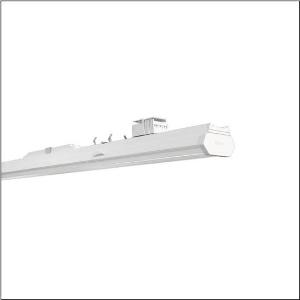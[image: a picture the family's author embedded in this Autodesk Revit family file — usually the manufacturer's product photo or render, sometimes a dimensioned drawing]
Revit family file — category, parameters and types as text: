
# Revit family: licross_r__21_protected_ho_52td11dn4axs_7332
name_source: partatom
category: Lighting Fixtures
units: mm (PartAtom-declared; Revit-internal decimal feet)

## family parameters
Cut with Voids When Loaded = No
Host = Face
Light Source = No
Part Type = Normal
Room Calculation Point = No
Round Connector Dimension = Use Diameter
Shared = No

## types (1)
- --- (1 x LED, 10000 lm, 55.1 W, 4000K)
    Apparent Load = 55 VA
    CIE Flux Codes = 84 94 98 99 100
    Color Rendering = 80
    Color Temperature = 4000K
    Default Elevation = 1800 mm
    Description = Licross® 21 Protected HO, luminaire insert, of sheet steel, galvanised, coil coated, white, length: 1.500mm, width: 90mm, height: 103mm, LED rated luminous flux: 10.000lm, light colour: 840, control gear: DALI 2, with plug, 5-pole, with phase selection, mains connection: 220..240V, AC, 50/60Hz, rated input power: 55W, halogen-free wiring, primary light control with lens, of plastic, primary optical cover: cover, of PMMA, light emission: direct distribution, primary light characteristic: symmetric, protection rating (complete): IP54, insulation class (complete): insulation class I (protective earthing), certification: CE, ENEC, VDE, UKCA, protection symbol: D if used in an environment with non-conductive dust loads with corresponding accessories, impact resistance: IK06, permissible ambient temperature for indoor applications: -25..+45°C, corresponds to IFS (International Featured Standards) requirements for safety and quality in the food industry, reducing of maximum allowable ambient temperature of 5°C with ceiling mounting, LABS conformity tested according to VDMA 24364:2018-05, packaging unit: 1 piece
    Height = 92 mm
    Lamp = 1 x LED
    Lamp Light Flux = 10000 lm
    Lamp Power = 55.1 W
    Lamp count = 1
    Length = 1500 mm
    Luminous efficacy = 181 lm/W
    Manufacturer = Siteco
    ModVariant = No
    Model = 52TD11DN4AXS
    Mounting Place = Ceiling
    Mounting Type = Pendant
    Number of Poles = 1
    OnlyDefault = Yes
    Power Factor = 1
    Product Name = Licross® 21 Protected HO
    Product group = luminaire insert
    ProductGroupID = 901
    Protection Class = Protection class I
    Protection Degree = IP 54
    RLX_Detail_Level = 1
    RLX_Emergency_Light_Flux = 0 lm
    RLX_Emergency_Type = 0
    RLX_Emergency_Type_DB = No
    RlxData = <blob elided: 24109 chars, md5=e7545ac7>
    Socket = socket
    Standby Power = 0 W
    System Light Flux = 10000 lm
    System Power = 55 W
    Type Comments = factory setting: luminous flux: 100 % | dim-lin: 254 | 316 mA
    Type Image = l_1256148.jpg
    URL = http://relux.com
    VarID = @adj_060119
    Voltage = 0 V
    Weight = 0.00 kg
    Width = 88 mm

## geometry (parser evidence)
native form markers: Blend x4, Sweep x10
no freeform markers — native parametric forms only
